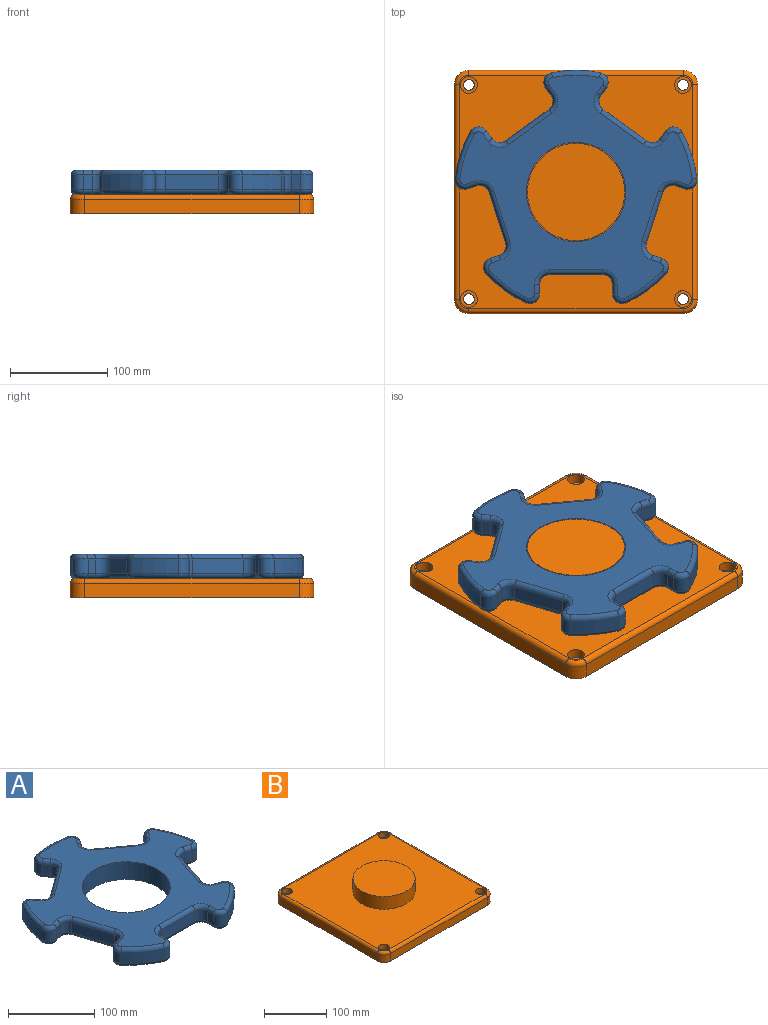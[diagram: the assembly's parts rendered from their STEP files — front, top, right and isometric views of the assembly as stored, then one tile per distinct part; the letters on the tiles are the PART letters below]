
ASSEMBLY  parts=2 mates=1
PART A: 123 faces, bbox 268.9x258.5x25 mm
  f0: plane 238.57x229.73mm, normal (0,0,1), area 21505.7mm2, adj f6,f43,f44,f45,f46,f47,f48,f49
  f1: plane 238.57x229.73mm, normal (0,0,-1), area 21505.7mm2, adj f6,f83,f84,f85,f86,f87,f88,f89
  f2: cylinder r=125mm len=40.68mm, axis (0,0,-1), area 759.5mm2, adj f13,f42,f51,f91
  f3: cylinder r=125mm len=47.82mm, axis (0,0,-1), area 759.5mm2, adj f35,f41,f67,f107
  f4: cylinder r=125mm len=50.29mm, axis (0,0,-1), area 759.5mm2, adj f28,f34,f82,f122
  f5: cylinder r=125mm len=47.82mm, axis (0,0,-1), area 759.5mm2, adj f21,f27,f66,f106
  f6: cylinder r=51mm len=102mm, axis (0,0,-1), area 8011.1mm2, adj f0,f1
  f7: cylinder r=125mm len=40.68mm, axis (0,0,-1), area 759.5mm2, adj f14,f20,f50,f90
  f8: plane 15x9.73mm, normal (-1,0,0), area 146mm2, adj f11,f14,f46,f86
  f9: plane 55x15mm, normal (0,-1,0), area 825mm2, adj f11,f12,f43,f83
  f10: plane 15x9.73mm, normal (1,0,0), area 146mm2, adj f12,f13,f47,f87
  f11: cylinder r=10mm len=15mm, axis (0,0,-1), area 235.6mm2, adj f8,f9,f44,f84
  f12: cylinder r=10mm len=15mm, axis (0,0,-1), area 235.6mm2, adj f9,f10,f45,f85
  f13: cylinder r=10mm len=15mm, axis (0,0,-1), area 299.5mm2, adj f2,f10,f49,f89
  f14: cylinder r=10mm len=15mm, axis (0,0,-1), area 299.5mm2, adj f7,f8,f48,f88
  f15: plane 15x9.26mm, normal (-0.31,-0.95,0), area 146mm2, adj f18,f21,f62,f102
  f16: plane 52.31x17mm, normal (0.95,-0.31,0), area 825mm2, adj f18,f19,f58,f98
  f17: plane 15x9.26mm, normal (0.31,0.95,0), area 146mm2, adj f19,f20,f54,f94
  f18: cylinder r=10mm len=15mm, axis (0,0,-1), area 235.6mm2, adj f15,f16,f60,f100
  f19: cylinder r=10mm len=15mm, axis (0,0,-1), area 235.6mm2, adj f16,f17,f56,f96
  f20: cylinder r=10mm len=16.25mm, axis (0,0,-1), area 299.5mm2, adj f7,f17,f52,f92
  f21: cylinder r=10mm len=15mm, axis (0,0,-1), area 299.5mm2, adj f5,f15,f64,f104
  f22: plane 15x7.87mm, normal (0.81,-0.59,0), area 146mm2, adj f25,f28,f78,f118
  f23: plane 44.5x32.33mm, normal (0.59,0.81,0), area 825mm2, adj f25,f26,f74,f114
  f24: plane 15x7.87mm, normal (-0.81,0.59,0), area 146mm2, adj f26,f27,f70,f110
  f25: cylinder r=10mm len=15mm, axis (0,0,-1), area 235.6mm2, adj f22,f23,f76,f116
  f26: cylinder r=10mm len=15mm, axis (0,0,-1), area 235.6mm2, adj f23,f24,f72,f112
  f27: cylinder r=10mm len=16.78mm, axis (0,0,-1), area 299.5mm2, adj f5,f24,f68,f108
  f28: cylinder r=10mm len=15.67mm, axis (0,0,-1), area 299.5mm2, adj f4,f22,f80,f120
  f29: plane 15x7.87mm, normal (0.81,0.59,0), area 146mm2, adj f32,f35,f71,f111
  f30: plane 44.5x32.33mm, normal (-0.59,0.81,0), area 825mm2, adj f32,f33,f75,f115
  f31: plane 15x7.87mm, normal (-0.81,-0.59,0), area 146mm2, adj f33,f34,f79,f119
  f32: cylinder r=10mm len=15mm, axis (0,0,-1), area 235.6mm2, adj f29,f30,f73,f113
  f33: cylinder r=10mm len=15mm, axis (0,0,-1), area 235.6mm2, adj f30,f31,f77,f117
  f34: cylinder r=10mm len=15.67mm, axis (0,0,-1), area 299.5mm2, adj f4,f31,f81,f121
  f35: cylinder r=10mm len=16.78mm, axis (0,0,-1), area 299.5mm2, adj f3,f29,f69,f109
  f36: plane 15x9.26mm, normal (-0.31,0.95,0), area 146mm2, adj f39,f42,f55,f95
  f37: plane 52.31x17mm, normal (-0.95,-0.31,0), area 825mm2, adj f39,f40,f59,f99
  f38: plane 15x9.26mm, normal (0.31,-0.95,0), area 146mm2, adj f40,f41,f63,f103
  f39: cylinder r=10mm len=15mm, axis (0,0,-1), area 235.6mm2, adj f36,f37,f57,f97
  f40: cylinder r=10mm len=15mm, axis (0,0,-1), area 235.6mm2, adj f37,f38,f61,f101
  f41: cylinder r=10mm len=15mm, axis (0,0,-1), area 299.5mm2, adj f3,f38,f65,f105
  f42: cylinder r=10mm len=16.25mm, axis (0,0,-1), area 299.5mm2, adj f2,f36,f53,f93
  f43: cylinder r=5mm len=55mm, axis (1,0,0), area 432mm2, adj f0,f9,f44,f45
  f44: torus R=15mm, axis (0,0,1), area 145.8mm2, adj f0,f11,f43,f46
  f45: torus R=15mm, axis (0,0,1), area 145.8mm2, adj f0,f12,f43,f47
  f46: cylinder r=5mm len=9.73mm, axis (0,-1,0), area 76.4mm2, adj f0,f8,f44,f48
  f47: cylinder r=5mm len=9.73mm, axis (0,1,0), area 76.4mm2, adj f0,f10,f45,f49
  f48: torus R=5mm, axis (0,0,1), area 128.3mm2, adj f0,f14,f46,f50
  f49: torus R=5mm, axis (0,0,1), area 128.3mm2, adj f0,f13,f47,f51
  f50: torus R=120mm, axis (0,0,1), area 391.9mm2, adj f0,f7,f48,f52
  f51: torus R=120mm, axis (0,0,1), area 391.9mm2, adj f0,f2,f49,f53
  f52: torus R=5mm, axis (0,0,1), area 128.3mm2, adj f0,f20,f50,f54
  f53: torus R=5mm, axis (0,0,1), area 128.3mm2, adj f0,f42,f51,f55
  f54: cylinder r=5mm len=10.8mm, axis (-0.95,0.31,0), area 76.4mm2, adj f0,f17,f52,f56
  f55: cylinder r=5mm len=10.8mm, axis (-0.95,-0.31,0), area 76.4mm2, adj f0,f36,f53,f57
  f56: torus R=15mm, axis (0,0,1), area 145.8mm2, adj f0,f19,f54,f58
  f57: torus R=15mm, axis (0,0,1), area 145.8mm2, adj f0,f39,f55,f59
  f58: cylinder r=5mm len=53.85mm, axis (0.31,0.95,0), area 432mm2, adj f0,f16,f56,f60
  f59: cylinder r=5mm len=53.85mm, axis (0.31,-0.95,0), area 432mm2, adj f0,f37,f57,f61
  f60: torus R=15mm, axis (0,0,1), area 145.8mm2, adj f0,f18,f58,f62
  f61: torus R=15mm, axis (0,0,1), area 145.8mm2, adj f0,f40,f59,f63
  f62: cylinder r=5mm len=10.8mm, axis (0.95,-0.31,0), area 76.4mm2, adj f0,f15,f60,f64
  f63: cylinder r=5mm len=10.8mm, axis (0.95,0.31,0), area 76.4mm2, adj f0,f38,f61,f65
  f64: torus R=5mm, axis (0,0,1), area 128.3mm2, adj f0,f21,f62,f66
  f65: torus R=5mm, axis (0,0,1), area 128.3mm2, adj f0,f41,f63,f67
  f66: torus R=120mm, axis (0,0,1), area 391.9mm2, adj f0,f5,f64,f68
  f67: torus R=120mm, axis (0,0,1), area 391.9mm2, adj f0,f3,f65,f69
  f68: torus R=5mm, axis (0,0,1), area 128.3mm2, adj f0,f27,f66,f70
  f69: torus R=5mm, axis (0,0,1), area 128.3mm2, adj f0,f35,f67,f71
  f70: cylinder r=5mm len=10.81mm, axis (-0.59,-0.81,0), area 76.4mm2, adj f0,f24,f68,f72
  f71: cylinder r=5mm len=10.81mm, axis (-0.59,0.81,0), area 76.4mm2, adj f0,f29,f69,f73
  f72: torus R=15mm, axis (0,0,1), area 145.8mm2, adj f0,f26,f70,f74
  f73: torus R=15mm, axis (0,0,1), area 145.8mm2, adj f0,f32,f71,f75
  f74: cylinder r=5mm len=47.44mm, axis (-0.81,0.59,0), area 432mm2, adj f0,f23,f72,f76
  f75: cylinder r=5mm len=47.44mm, axis (-0.81,-0.59,0), area 432mm2, adj f0,f30,f73,f77
  f76: torus R=15mm, axis (0,0,1), area 145.8mm2, adj f0,f25,f74,f78
  f77: torus R=15mm, axis (0,0,1), area 145.8mm2, adj f0,f33,f75,f79
  f78: cylinder r=5mm len=10.81mm, axis (0.59,0.81,0), area 76.4mm2, adj f0,f22,f76,f80
  f79: cylinder r=5mm len=10.81mm, axis (0.59,-0.81,0), area 76.4mm2, adj f0,f31,f77,f81
  f80: torus R=5mm, axis (0,0,1), area 128.3mm2, adj f0,f28,f78,f82
  f81: torus R=5mm, axis (0,0,1), area 128.3mm2, adj f0,f34,f79,f82
  f82: torus R=120mm, axis (0,0,1), area 391.9mm2, adj f0,f4,f80,f81
  f83: cylinder r=5mm len=55mm, axis (-1,0,0), area 432mm2, adj f1,f9,f84,f85
  f84: torus R=15mm, axis (0,0,1), area 145.8mm2, adj f1,f11,f83,f86
  f85: torus R=15mm, axis (0,0,1), area 145.8mm2, adj f1,f12,f83,f87
  f86: cylinder r=5mm len=9.73mm, axis (0,1,0), area 76.4mm2, adj f1,f8,f84,f88
  f87: cylinder r=5mm len=9.73mm, axis (0,-1,0), area 76.4mm2, adj f1,f10,f85,f89
  f88: torus R=5mm, axis (0,0,1), area 128.3mm2, adj f1,f14,f86,f90
  f89: torus R=5mm, axis (0,0,1), area 128.3mm2, adj f1,f13,f87,f91
  f90: torus R=120mm, axis (0,0,1), area 391.9mm2, adj f1,f7,f88,f92
  f91: torus R=120mm, axis (0,0,1), area 391.9mm2, adj f1,f2,f89,f93
  f92: torus R=5mm, axis (0,0,1), area 128.3mm2, adj f1,f20,f90,f94
  f93: torus R=5mm, axis (0,0,1), area 128.3mm2, adj f1,f42,f91,f95
  f94: cylinder r=5mm len=10.8mm, axis (0.95,-0.31,0), area 76.4mm2, adj f1,f17,f92,f96
  f95: cylinder r=5mm len=10.8mm, axis (0.95,0.31,0), area 76.4mm2, adj f1,f36,f93,f97
  f96: torus R=15mm, axis (0,0,1), area 145.8mm2, adj f1,f19,f94,f98
  f97: torus R=15mm, axis (0,0,1), area 145.8mm2, adj f1,f39,f95,f99
  f98: cylinder r=5mm len=53.85mm, axis (-0.31,-0.95,0), area 432mm2, adj f1,f16,f96,f100
  f99: cylinder r=5mm len=53.85mm, axis (-0.31,0.95,0), area 432mm2, adj f1,f37,f97,f101
  f100: torus R=15mm, axis (0,0,1), area 145.8mm2, adj f1,f18,f98,f102
  f101: torus R=15mm, axis (0,0,1), area 145.8mm2, adj f1,f40,f99,f103
  f102: cylinder r=5mm len=10.8mm, axis (-0.95,0.31,0), area 76.4mm2, adj f1,f15,f100,f104
  f103: cylinder r=5mm len=10.8mm, axis (-0.95,-0.31,0), area 76.4mm2, adj f1,f38,f101,f105
  f104: torus R=5mm, axis (0,0,1), area 128.3mm2, adj f1,f21,f102,f106
  f105: torus R=5mm, axis (0,0,1), area 128.3mm2, adj f1,f41,f103,f107
  f106: torus R=120mm, axis (0,0,1), area 391.9mm2, adj f1,f5,f104,f108
  f107: torus R=120mm, axis (0,0,1), area 391.9mm2, adj f1,f3,f105,f109
  f108: torus R=5mm, axis (0,0,1), area 128.3mm2, adj f1,f27,f106,f110
  f109: torus R=5mm, axis (0,0,1), area 128.3mm2, adj f1,f35,f107,f111
  f110: cylinder r=5mm len=10.81mm, axis (0.59,0.81,0), area 76.4mm2, adj f1,f24,f108,f112
  f111: cylinder r=5mm len=10.81mm, axis (0.59,-0.81,0), area 76.4mm2, adj f1,f29,f109,f113
  f112: torus R=15mm, axis (0,0,1), area 145.8mm2, adj f1,f26,f110,f114
  f113: torus R=15mm, axis (0,0,1), area 145.8mm2, adj f1,f32,f111,f115
  f114: cylinder r=5mm len=47.44mm, axis (0.81,-0.59,0), area 432mm2, adj f1,f23,f112,f116
  f115: cylinder r=5mm len=47.44mm, axis (0.81,0.59,0), area 432mm2, adj f1,f30,f113,f117
  f116: torus R=15mm, axis (0,0,1), area 145.8mm2, adj f1,f25,f114,f118
  f117: torus R=15mm, axis (0,0,1), area 145.8mm2, adj f1,f33,f115,f119
  f118: cylinder r=5mm len=10.81mm, axis (-0.59,-0.81,0), area 76.4mm2, adj f1,f22,f116,f120
  f119: cylinder r=5mm len=10.81mm, axis (-0.59,0.81,0), area 76.4mm2, adj f1,f31,f117,f121
  f120: torus R=5mm, axis (0,0,1), area 128.3mm2, adj f1,f28,f118,f122
  f121: torus R=5mm, axis (0,0,1), area 128.3mm2, adj f1,f34,f119,f122
  f122: torus R=120mm, axis (0,0,1), area 391.9mm2, adj f1,f4,f120,f121
PART B: 32 faces, bbox 252.5x252.5x45 mm
  f0: plane 220x15mm, normal (1,0,0), area 3300mm2, adj f5,f8,f11,f27
  f1: plane 220x15mm, normal (0,1,0), area 3300mm2, adj f5,f8,f9,f31
  f2: plane 220x15mm, normal (-1,0,0), area 3300mm2, adj f5,f9,f10,f28
  f3: plane 220x15mm, normal (0,-1,0), area 3300mm2, adj f5,f10,f11,f24
  f4: plane 240x240mm, normal (0,0,1), area 48725.4mm2, adj f6,f14,f17,f20,f23,f24,f25,f26
  f5: plane 250x250mm, normal (0,0,-1), area 61926.7mm2, adj f0,f1,f2,f3,f8,f9,f10,f11
  f6: cylinder r=50mm len=100mm, axis (0,0,-1), area 7854mm2, adj f4,f7
  f7: plane 100x100mm, normal (0,0,1), area 7854mm2, adj f6
  f8: cylinder r=15mm len=15mm, axis (0,0,-1), area 353.4mm2, adj f0,f1,f5,f29
  f9: cylinder r=15mm len=15mm, axis (0,0,1), area 353.4mm2, adj f1,f2,f5,f30
  f10: cylinder r=15mm len=15mm, axis (0,0,-1), area 353.4mm2, adj f2,f3,f5,f26
  f11: cylinder r=15mm len=15mm, axis (0,0,1), area 353.4mm2, adj f0,f3,f5,f25
  f12: cylinder r=5.5mm len=11mm, axis (0,0,1), area 345.6mm2, adj f5,f13
  f13: plane 17.25x17.25mm, normal (0,0,1), area 138.7mm2, adj f12,f14
  f14: cylinder r=8.62mm len=17.25mm, axis (0,0,1), area 541.9mm2, adj f4,f13
  f15: cylinder r=5.5mm len=11mm, axis (0,0,1), area 345.6mm2, adj f5,f16
  f16: plane 17.25x17.25mm, normal (0,0,1), area 138.7mm2, adj f15,f17
  f17: cylinder r=8.62mm len=17.25mm, axis (0,0,1), area 541.9mm2, adj f4,f16
  f18: cylinder r=5.5mm len=11mm, axis (0,0,1), area 345.6mm2, adj f5,f19
  f19: plane 17.25x17.25mm, normal (0,0,1), area 138.7mm2, adj f18,f20
  f20: cylinder r=8.62mm len=17.25mm, axis (0,0,1), area 541.9mm2, adj f4,f19
  f21: cylinder r=5.5mm len=11mm, axis (0,0,1), area 345.6mm2, adj f5,f22
  f22: plane 17.25x17.25mm, normal (0,0,1), area 138.7mm2, adj f21,f23
  f23: cylinder r=8.62mm len=17.25mm, axis (0,0,1), area 541.9mm2, adj f4,f22
  f24: cylinder r=5mm len=220mm, axis (-1,0,0), area 1727.9mm2, adj f3,f4,f25,f26
  f25: torus R=10mm, axis (0,0,1), area 162.6mm2, adj f4,f11,f24,f27
  f26: torus R=10mm, axis (0,0,1), area 162.6mm2, adj f4,f10,f24,f28
  f27: cylinder r=5mm len=220mm, axis (0,-1,0), area 1727.9mm2, adj f0,f4,f25,f29
  f28: cylinder r=5mm len=220mm, axis (0,1,0), area 1727.9mm2, adj f2,f4,f26,f30
  f29: torus R=10mm, axis (0,0,1), area 162.6mm2, adj f4,f8,f27,f31
  f30: torus R=10mm, axis (0,0,1), area 162.6mm2, adj f4,f9,f28,f31
  f31: cylinder r=5mm len=220mm, axis (1,0,0), area 1727.9mm2, adj f1,f4,f29,f30
PLACE A t=(161.03,36.31,-107.49)mm
PLACE B t=(161.03,36.31,-107.49)mm
MATE revolute B.f6 <-> A.f2  axis (0,0,-1) through (161.03,36.31,-62.49)mm
